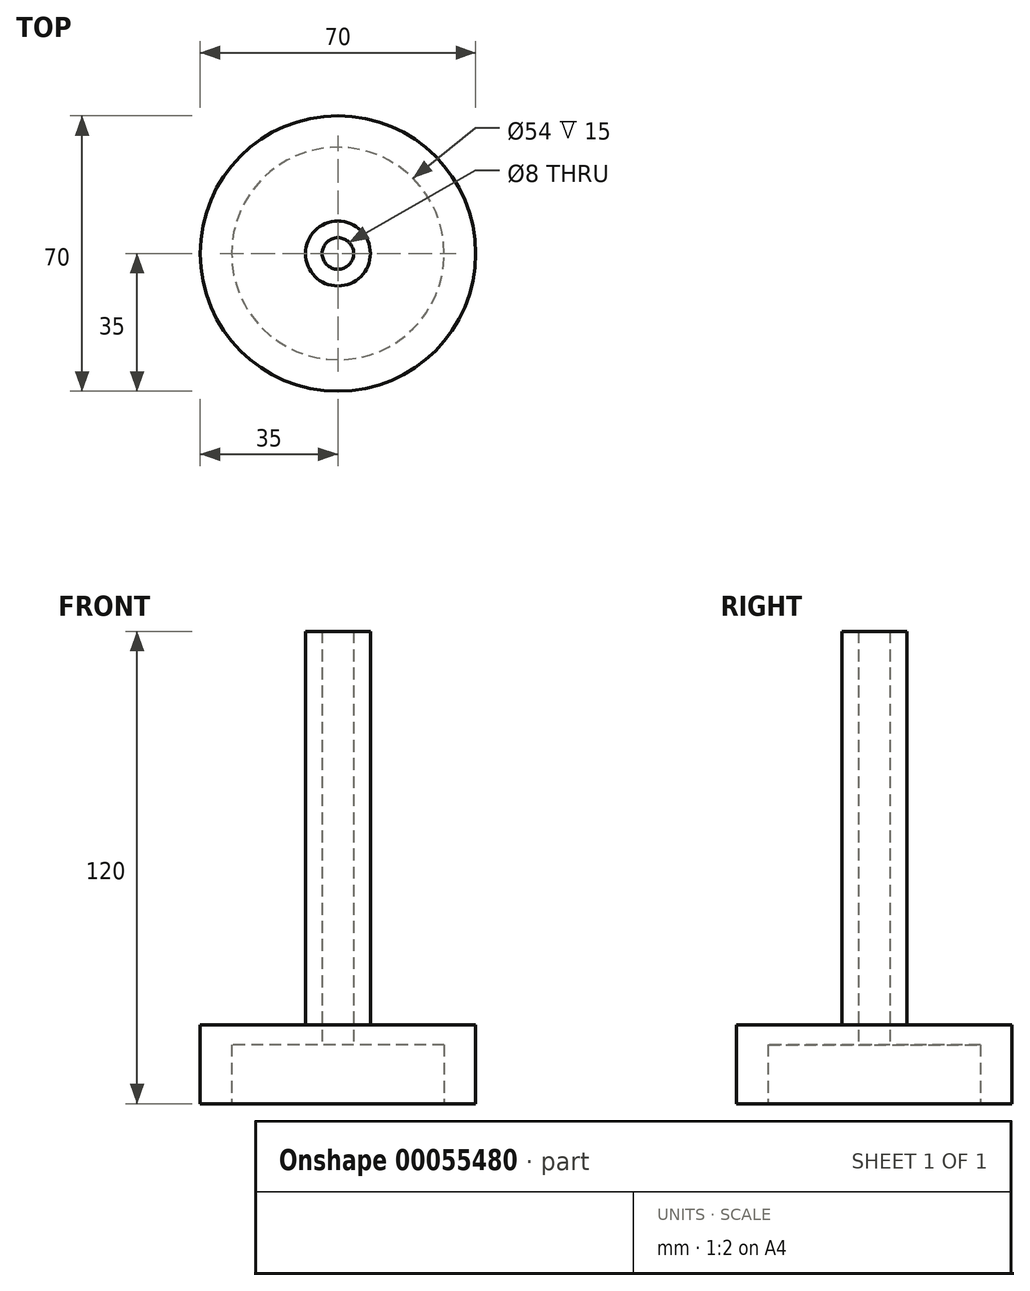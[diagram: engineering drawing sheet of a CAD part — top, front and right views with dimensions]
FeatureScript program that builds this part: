
annotation { "Feature Type Name" : "Feature", "Feature Type Description" : "" }
export const myFeature = defineFeature(function(context is Context, id is Id, definition is map)
    precondition{}
    {
        {
            var Q0;
            Q0=qCreatedBy(makeId("Top.planeOp"),FACE);
            var sketch = newSketch(context, id + "F0", { "sketchPlane" : qUnion([Q0])});
            skCircle(sketch, "E0", {"center": v(0, 0) * mm, "radius": 35 * mm});
            skCircle(sketch, "E1", {"center": v(0, 0) * mm, "radius": 27 * mm});
            skSolve(sketch);
        }
        {
            var Q0;
            Q0=makeQuery(id+"F0.imprint","IMPRINT",FACE,{"disambiguationData":[TD([[makeQuery(id+"F0.imprint","IMPRINT",EDGE,{"derivedFrom":sQuery(id+"F0.wireOp",EDGE,"E0")}),1.0]])]});
            extrude(context, id + "F1", {"entities" : qUnion([Q0]), "depth" : 20 * mm});
        }
        {
            var Q0;
            Q0=makeQuery(id+"F0.imprint","IMPRINT",FACE,{"disambiguationData":[TD([[makeQuery(id+"F0.imprint","IMPRINT",EDGE,{"derivedFrom":sQuery(id+"F0.wireOp",EDGE,"E1")}),1.0]])]});
            extrude(context, id + "F2", {"entities" : qUnion([Q0]), "operationType" : NewBodyOperationType.ADD, "depth" : 20 * mm, "hasSecondDirection" : true, "secondDirectionOppositeDirection" : false, "secondDirectionDepth" : 15 * mm});
        }
        {
            var Q0;
            {var subQ0=sQuery(id+"F0.wireOp",EDGE,"E1");Q0=makeQuery(id+"F2.boolean.opBoolean","MERGE",FACE,{"derivedFrom":[makeQuery(id+"F1.opExtrude","CAP_FACE",FACE,{"disambiguationData":[OSD([sQuery(id+"F0.wireOp",EDGE,"E0"),subQ0])],"isStart":false}),makeQuery(id+"F2.opExtrude","CAP_FACE",FACE,{"disambiguationData":[OSD([subQ0])],"isStart":false})]});}
            var sketch = newSketch(context, id + "F3", { "sketchPlane" : qUnion([Q0])});
            skCircle(sketch, "E2", {"center": v(0, 0) * mm, "radius": 8.25 * mm});
            skCircle(sketch, "E3", {"center": v(0, 0) * mm, "radius": 4 * mm});
            skSolve(sketch);
        }
        {
            var Q0;
            Q0=makeQuery(id+"F3.imprint","IMPRINT",FACE,{"disambiguationData":[TD([[makeQuery(id+"F3.imprint","IMPRINT",EDGE,{"derivedFrom":sQuery(id+"F3.wireOp",EDGE,"E2")}),1.0]])]});
            extrude(context, id + "F4", {"entities" : qUnion([Q0]), "operationType" : NewBodyOperationType.ADD, "depth" : 100 * mm});
        }
        {
            var Q0;
            {var subQ0=sQuery(id+"F0.wireOp",EDGE,"E1");Q0=makeQuery(id+"F4.boolean.opBoolean","SPLIT",FACE,{"disambiguationData":[TD([makeQuery(id+"F4.opExtrude","SWEPT_FACE",FACE,{"disambiguationData":[OSD([sQuery(id+"F3.wireOp",EDGE,"E3")])]})])],"derivedFrom":makeQuery(id+"F2.boolean.opBoolean","MERGE",FACE,{"derivedFrom":[makeQuery(id+"F1.opExtrude","CAP_FACE",FACE,{"disambiguationData":[OSD([sQuery(id+"F0.wireOp",EDGE,"E0"),subQ0])],"isStart":false}),makeQuery(id+"F2.opExtrude","CAP_FACE",FACE,{"disambiguationData":[OSD([subQ0])],"isStart":false})]})});}
            extrude(context, id + "F5", {"entities" : qUnion([Q0]), "operationType" : NewBodyOperationType.REMOVE, "oppositeDirection" : true, "depth" : 12 * mm});
        }
    });
